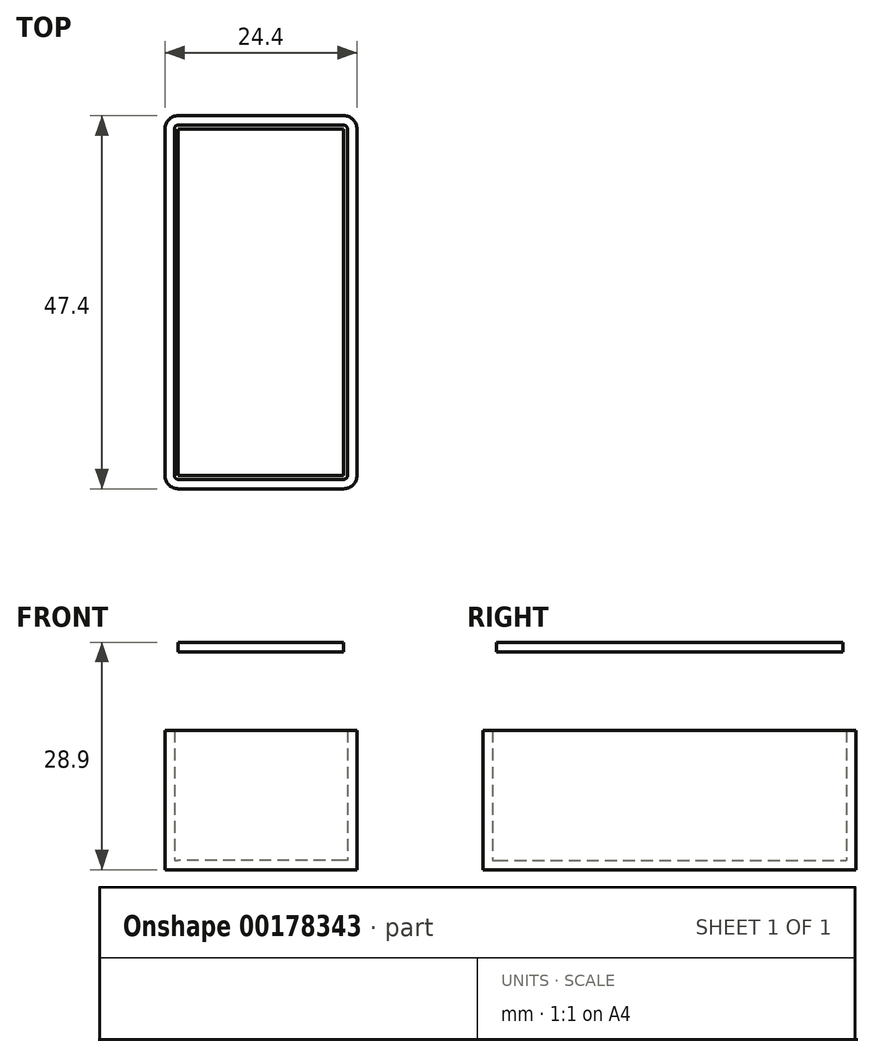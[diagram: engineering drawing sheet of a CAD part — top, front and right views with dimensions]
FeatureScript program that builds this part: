
annotation { "Feature Type Name" : "Feature", "Feature Type Description" : "" }
export const myFeature = defineFeature(function(context is Context, id is Id, definition is map)
    precondition{}
    {
        {
            var Q0;
            Q0=qCreatedBy(makeId("Top.planeOp"),FACE);
            var sketch = newSketch(context, id + "F0", { "sketchPlane" : qUnion([Q0])});
            skLineSegment(sketch, "E0.bottom", {"start": v(10.5, -22.5) * mm, "end": v(-10.5, -22.5) * mm});
            skLineSegment(sketch, "E0.top", {"start": v(10.5, 22.5) * mm, "end": v(-10.5, 22.5) * mm});
            skLineSegment(sketch, "E0.left", {"start": v(11, -22) * mm, "end": v(11, 22) * mm});
            skLineSegment(sketch, "E0.right", {"start": v(-11, -22) * mm, "end": v(-11, 22) * mm});
            skPoint(sketch, "E0.middle", {"position": v(0, 0) * mm});
            skPoint(sketch, "E1.visualSharp", {"position": v(-11, 22.5) * mm});
            skArc(sketch, "E1.filletArc", {"start": v(-10.5, 22.5) * mm, "mid": v(-10.85, 22.35) * mm, "end": v(-11, 22) * mm});
            skPoint(sketch, "E2.visualSharp", {"position": v(11, 22.5) * mm});
            skArc(sketch, "E2.filletArc", {"start": v(11, 22) * mm, "mid": v(10.85, 22.35) * mm, "end": v(10.5, 22.5) * mm});
            skPoint(sketch, "E3.visualSharp", {"position": v(11, -22.5) * mm});
            skArc(sketch, "E3.filletArc", {"start": v(10.5, -22.5) * mm, "mid": v(10.85, -22.35) * mm, "end": v(11, -22) * mm});
            skPoint(sketch, "E4.visualSharp", {"position": v(-11, -22.5) * mm});
            skArc(sketch, "E4.filletArc", {"start": v(-11, -22) * mm, "mid": v(-10.85, -22.35) * mm, "end": v(-10.5, -22.5) * mm});
            skArc(sketch, "E5.0", {"start": v(-12.2, -22) * mm, "mid": v(-11.7, -23.2) * mm, "end": v(-10.5, -23.7) * mm});
            skLineSegment(sketch, "E5.1", {"start": v(10.5, -23.7) * mm, "end": v(-10.5, -23.7) * mm});
            skLineSegment(sketch, "E5.2", {"start": v(-12.2, -22) * mm, "end": v(-12.2, 22) * mm});
            skArc(sketch, "E5.3", {"start": v(10.5, -23.7) * mm, "mid": v(11.7, -23.2) * mm, "end": v(12.2, -22) * mm});
            skArc(sketch, "E5.4", {"start": v(-10.5, 23.7) * mm, "mid": v(-11.7, 23.2) * mm, "end": v(-12.2, 22) * mm});
            skLineSegment(sketch, "E5.5", {"start": v(10.5, 23.7) * mm, "end": v(-10.5, 23.7) * mm});
            skArc(sketch, "E5.6", {"start": v(12.2, 22) * mm, "mid": v(11.7, 23.2) * mm, "end": v(10.5, 23.7) * mm});
            skLineSegment(sketch, "E5.7", {"start": v(12.2, -22) * mm, "end": v(12.2, 22) * mm});
            skSolve(sketch);
        }
        {
            var Q0;
            Q0 = qSketchRegion(id + "F0", true);
            var Q1;
            Q1=makeQuery(id+"F0.imprint","IMPRINT",FACE,{"disambiguationData":[TD([[makeQuery(id+"F0.imprint","IMPRINT",EDGE,{"derivedFrom":sQuery(id+"F0.wireOp",EDGE,"E0.bottom")}),-1.0]])]});
            extrude(context, id + "F1", {"entities" : qUnion([Q0, Q1]), "oppositeDirection" : true, "depth" : 1.2 * mm});
        }
        {
            var Q0;
            Q0=makeQuery(id+"F0.imprint","IMPRINT",FACE,{"disambiguationData":[TD([[makeQuery(id+"F0.imprint","IMPRINT",EDGE,{"derivedFrom":sQuery(id+"F0.wireOp",EDGE,"E0.bottom")}),1.0]])]});
            extrude(context, id + "F2", {"entities" : qUnion([Q0]), "operationType" : NewBodyOperationType.ADD, "depth" : 16.5 * mm});
        }
        {
            var Q0;
            Q0=makeQuery(id+"F2.opExtrude","CAP_FACE",FACE,{"disambiguationData":[OSD([sQuery(id+"F0.wireOp",EDGE,"E0.bottom"),sQuery(id+"F0.wireOp",EDGE,"E0.top"),sQuery(id+"F0.wireOp",EDGE,"E0.left"),sQuery(id+"F0.wireOp",EDGE,"E0.right"),sQuery(id+"F0.wireOp",EDGE,"E1.filletArc"),sQuery(id+"F0.wireOp",EDGE,"E2.filletArc"),sQuery(id+"F0.wireOp",EDGE,"E3.filletArc"),sQuery(id+"F0.wireOp",EDGE,"E4.filletArc"),sQuery(id+"F0.wireOp",EDGE,"E5.0"),sQuery(id+"F0.wireOp",EDGE,"E5.1"),sQuery(id+"F0.wireOp",EDGE,"E5.2"),sQuery(id+"F0.wireOp",EDGE,"E5.3"),sQuery(id+"F0.wireOp",EDGE,"E5.4"),sQuery(id+"F0.wireOp",EDGE,"E5.5"),sQuery(id+"F0.wireOp",EDGE,"E5.6"),sQuery(id+"F0.wireOp",EDGE,"E5.7")])],"isStart":false});
            cPlane(context, id + "F3", {"entities" : qUnion([Q0]), "cplaneType" : CPlaneType.OFFSET, "offset" : 10 * mm, "width" : 150 * mm, "height" : 150 * mm});
        }
        {
            var Q0;
            Q0=qCreatedBy(id+"F3.planeOp",FACE);
            var sketch = newSketch(context, id + "F4", { "sketchPlane" : qUnion([Q0])});
            skLineSegment(sketch, "E6.0", {"start": v(10.5, 22) * mm, "end": v(-10.5, 22) * mm});
            skLineSegment(sketch, "E6.1", {"start": v(10.5, -22) * mm, "end": v(10.5, 22) * mm});
            skLineSegment(sketch, "E6.2", {"start": v(10.5, -22) * mm, "end": v(-10.5, -22) * mm});
            skLineSegment(sketch, "E6.3", {"start": v(-10.5, -22) * mm, "end": v(-10.5, 22) * mm});
            skSolve(sketch);
        }
        {
            var Q0;
            Q0=makeQuery(id+"F4.imprint","IMPRINT",FACE,{"disambiguationData":[TD([[makeQuery(id+"F4.imprint","IMPRINT",EDGE,{"derivedFrom":sQuery(id+"F4.wireOp",EDGE,"E6.0")}),1.0]])]});
            extrude(context, id + "F5", {"entities" : qUnion([Q0]), "depth" : 1.2 * mm});
        }
    });
